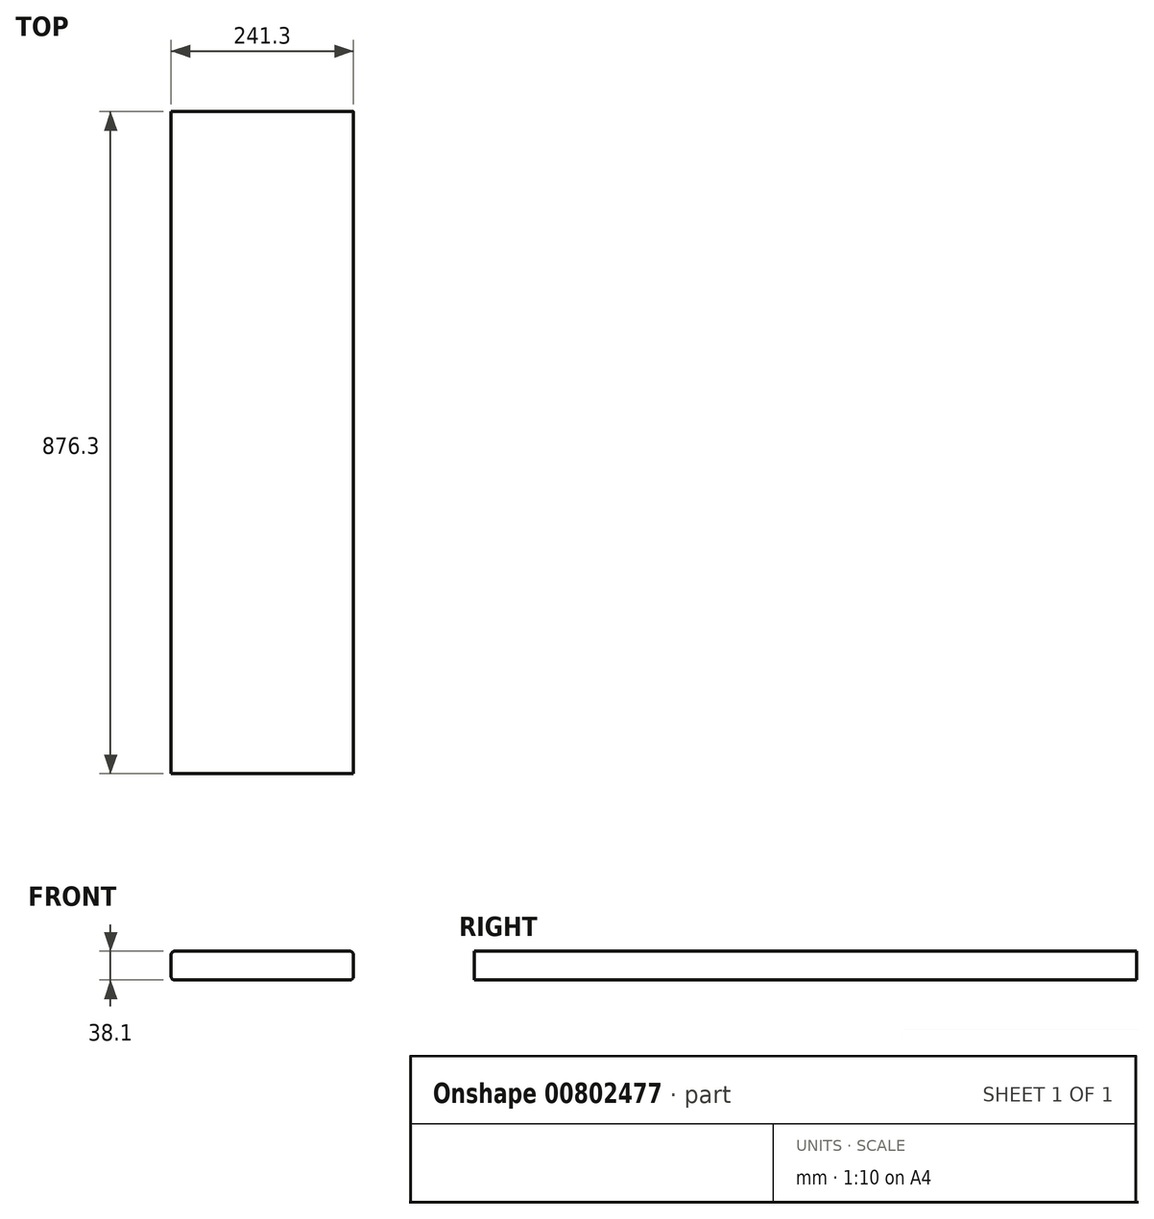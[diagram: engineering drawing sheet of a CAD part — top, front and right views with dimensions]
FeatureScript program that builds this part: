
annotation { "Feature Type Name" : "Feature", "Feature Type Description" : "" }
export const myFeature = defineFeature(function(context is Context, id is Id, definition is map)
    precondition{}
    {
        {
            var Q0;
            Q0=qCreatedBy(makeId("Front.planeOp"),FACE);
            var sketch = newSketch(context, id + "F0", { "sketchPlane" : qUnion([Q0])});
            skLineSegment(sketch, "E0.bottom", {"start": v(-115.82, 19.05) * mm, "end": v(115.82, 19.05) * mm});
            skLineSegment(sketch, "E0.top", {"start": v(-115.82, -19.05) * mm, "end": v(115.82, -19.05) * mm});
            skLineSegment(sketch, "E0.left", {"start": v(-120.65, 14.22) * mm, "end": v(-120.65, -14.22) * mm});
            skLineSegment(sketch, "E0.right", {"start": v(120.65, 14.22) * mm, "end": v(120.65, -14.22) * mm});
            skPoint(sketch, "E0.middle", {"position": v(0, 0) * mm});
            skPoint(sketch, "E1.visualSharp", {"position": v(-120.65, 19.05) * mm});
            skArc(sketch, "E1.filletArc", {"start": v(-115.82, 19.05) * mm, "mid": v(-119.24, 17.64) * mm, "end": v(-120.65, 14.22) * mm});
            skPoint(sketch, "E2.visualSharp", {"position": v(120.65, 19.05) * mm});
            skArc(sketch, "E2.filletArc", {"start": v(120.65, 14.22) * mm, "mid": v(119.24, 17.64) * mm, "end": v(115.82, 19.05) * mm});
            skPoint(sketch, "E3.visualSharp", {"position": v(120.65, -19.05) * mm});
            skArc(sketch, "E3.filletArc", {"start": v(115.82, -19.05) * mm, "mid": v(119.24, -17.64) * mm, "end": v(120.65, -14.22) * mm});
            skPoint(sketch, "E4.visualSharp", {"position": v(-120.65, -19.05) * mm});
            skArc(sketch, "E4.filletArc", {"start": v(-120.65, -14.22) * mm, "mid": v(-119.24, -17.64) * mm, "end": v(-115.82, -19.05) * mm});
            skSolve(sketch);
        }
        {
            var Q0;
            Q0=makeQuery(id+"F0.imprint","IMPRINT",FACE,{"disambiguationData":[TD([[makeQuery(id+"F0.imprint","IMPRINT",EDGE,{"derivedFrom":sQuery(id+"F0.wireOp",EDGE,"E0.bottom")}),-1.0]])]});
            extrude(context, id + "F1", {"entities" : qUnion([Q0]), "endBound" : BoundingType.SYMMETRIC, "depth" : 876.3 * mm, "offsetDistance" : 25.4 * mm});
        }
    });
